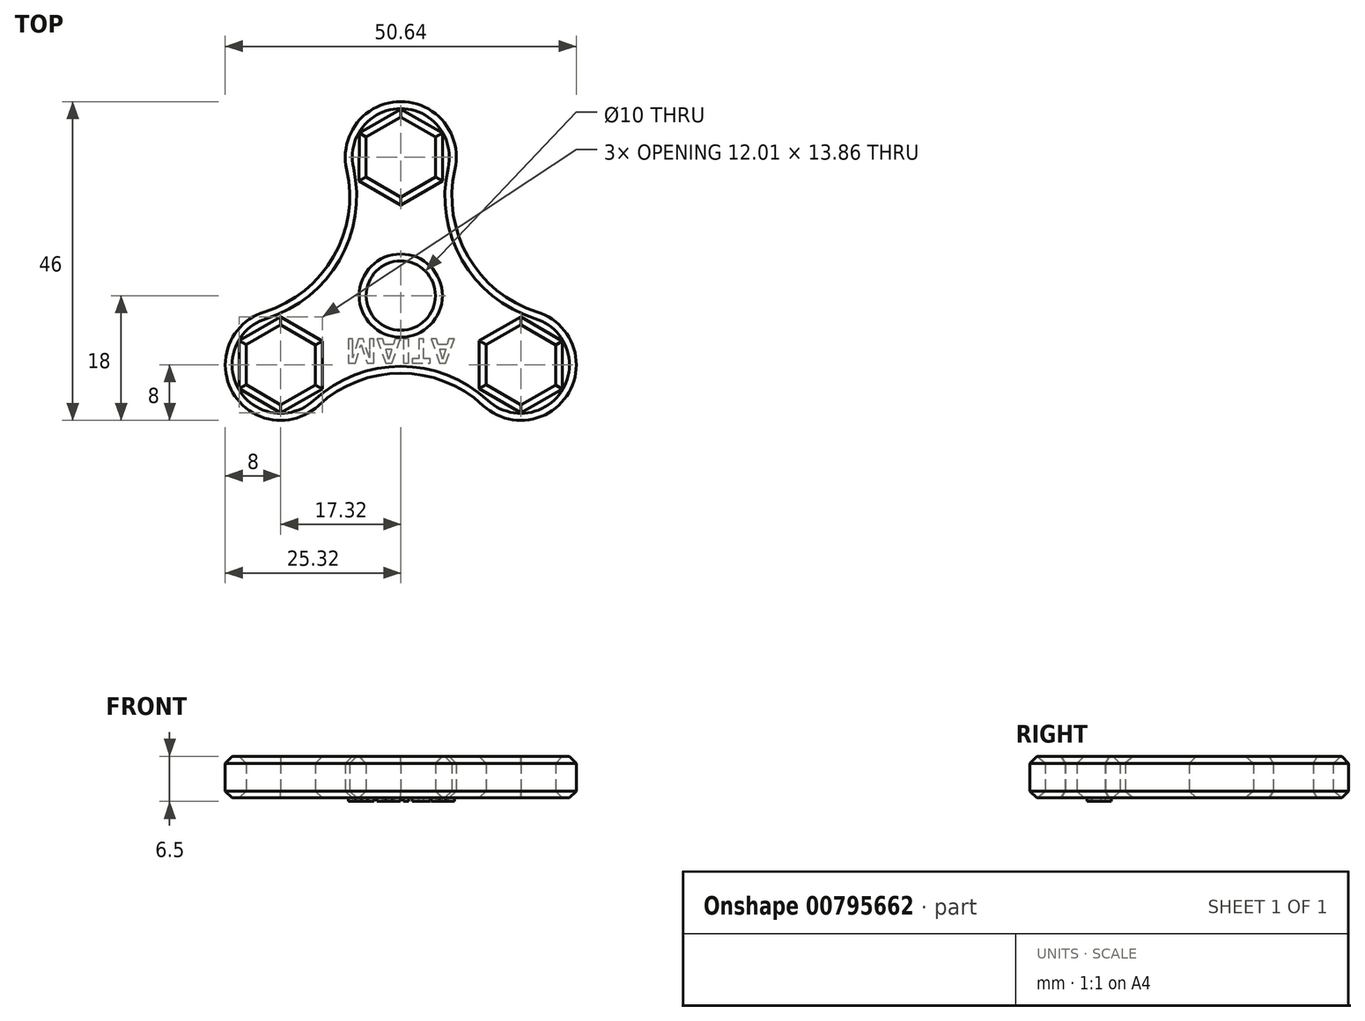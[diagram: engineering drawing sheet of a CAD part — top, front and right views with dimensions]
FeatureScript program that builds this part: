
annotation { "Feature Type Name" : "Feature", "Feature Type Description" : "" }
export const myFeature = defineFeature(function(context is Context, id is Id, definition is map)
    precondition{}
    {
        {
            var Q0;
            Q0=qCreatedBy(makeId("Top.planeOp"),FACE);
            var sketch = newSketch(context, id + "F0", { "sketchPlane" : qUnion([Q0])});
            skCircle(sketch, "E0", {"center": v(0, 0) * mm, "radius": 20 * mm, "construction": true});
            skCircle(sketch, "E1", {"center": v(0, 0) * mm, "radius": 5 * mm});
            skCircle(sketch, "E2.cCircle", {"center": v(0, 20) * mm, "radius": 5 * mm, "construction": true});
            skLineSegment(sketch, "E2.0", {"start": v(0, 25.77) * mm, "end": v(5, 22.88) * mm});
            skLineSegment(sketch, "E2.1", {"start": v(5, 22.88) * mm, "end": v(5, 17.1) * mm});
            skLineSegment(sketch, "E2.2", {"start": v(5, 17.1) * mm, "end": v(0, 14.23) * mm});
            skLineSegment(sketch, "E2.3", {"start": v(0, 14.23) * mm, "end": v(-5, 17.12) * mm});
            skLineSegment(sketch, "E2.4", {"start": v(-5, 17.12) * mm, "end": v(-5, 22.9) * mm});
            skLineSegment(sketch, "E2.5", {"start": v(-5, 22.9) * mm, "end": v(0, 25.77) * mm});
            skPoint(sketch, "E2.0.midPoint", {"position": v(2.5, 24.33) * mm});
            skCircle(sketch, "E3", {"center": v(0, 20) * mm, "radius": 8 * mm});
            skCircle(sketch, "E4", {"center": v(0, 0) * mm, "radius": 8 * mm});
            skCircle(sketch, "E5.1.0", {"center": v(-17.32, -10) * mm, "radius": 8 * mm});
            skLineSegment(sketch, "E5.1.1", {"start": v(-17.33, -15.77) * mm, "end": v(-22.32, -12.88) * mm});
            skLineSegment(sketch, "E5.1.2", {"start": v(-12.32, -12.9) * mm, "end": v(-17.33, -15.77) * mm});
            skLineSegment(sketch, "E5.1.3", {"start": v(-12.32, -7.12) * mm, "end": v(-12.32, -12.9) * mm});
            skLineSegment(sketch, "E5.1.4", {"start": v(-17.31, -4.23) * mm, "end": v(-12.32, -7.12) * mm});
            skLineSegment(sketch, "E5.1.5", {"start": v(-22.32, -7.1) * mm, "end": v(-17.31, -4.23) * mm});
            skLineSegment(sketch, "E5.1.6", {"start": v(-22.32, -12.88) * mm, "end": v(-22.32, -7.1) * mm});
            skCircle(sketch, "E5.2.0", {"center": v(17.32, -10) * mm, "radius": 8 * mm});
            skLineSegment(sketch, "E5.2.1", {"start": v(22.32, -7.12) * mm, "end": v(22.32, -12.9) * mm});
            skLineSegment(sketch, "E5.2.2", {"start": v(17.33, -4.23) * mm, "end": v(22.32, -7.12) * mm});
            skLineSegment(sketch, "E5.2.3", {"start": v(12.32, -7.1) * mm, "end": v(17.33, -4.23) * mm});
            skLineSegment(sketch, "E5.2.4", {"start": v(12.32, -12.88) * mm, "end": v(12.32, -7.1) * mm});
            skLineSegment(sketch, "E5.2.5", {"start": v(17.31, -15.77) * mm, "end": v(12.32, -12.88) * mm});
            skLineSegment(sketch, "E5.2.6", {"start": v(22.32, -12.9) * mm, "end": v(17.31, -15.77) * mm});
            skArc(sketch, "E6", {"start": v(-19.69, -2.36) * mm, "mid": v(-9.71, 5.6) * mm, "end": v(-7.8, 18.23) * mm});
            skArc(sketch, "E7.1.0", {"start": v(11.89, -15.87) * mm, "mid": v(0, -11.21) * mm, "end": v(-11.89, -15.87) * mm});
            skArc(sketch, "E7.2.0", {"start": v(7.8, 18.23) * mm, "mid": v(9.71, 5.6) * mm, "end": v(19.69, -2.36) * mm});
            skSolve(sketch);
        }
        {
            var Q0;
            Q0=makeQuery(id+"F0.imprint","IMPRINT",FACE,{"disambiguationData":[TD([[makeQuery(id+"F0.imprint","IMPRINT",EDGE,{"derivedFrom":sQuery(id+"F0.wireOp",EDGE,"E5.1.1")}),1.0]])]});
            var Q1;
            Q1=makeQuery(id+"F0.imprint","IMPRINT",FACE,{"disambiguationData":[TD([[makeQuery(id+"F0.imprint","IMPRINT",EDGE,{"derivedFrom":sQuery(id+"F0.wireOp",EDGE,"E4")}),-1.0]])]});
            var Q2;
            Q2=makeQuery(id+"F0.imprint","IMPRINT",FACE,{"disambiguationData":[TD([[makeQuery(id+"F0.imprint","IMPRINT",EDGE,{"derivedFrom":sQuery(id+"F0.wireOp",EDGE,"E1")}),-1.0]])]});
            var Q3;
            Q3=makeQuery(id+"F0.imprint","IMPRINT",FACE,{"disambiguationData":[TD([[makeQuery(id+"F0.imprint","IMPRINT",EDGE,{"derivedFrom":sQuery(id+"F0.wireOp",EDGE,"E5.2.1")}),1.0]])]});
            var Q4;
            Q4=makeQuery(id+"F0.imprint","IMPRINT",FACE,{"disambiguationData":[TD([[makeQuery(id+"F0.imprint","IMPRINT",EDGE,{"derivedFrom":sQuery(id+"F0.wireOp",EDGE,"E2.0")}),1.0]])]});
            extrude(context, id + "F1", {"entities" : qUnion([Q0, Q1, Q2, Q3, Q4]), "depth" : 6 * mm, "offsetDistance" : 25 * mm});
        }
        {
            var Q0;
            Q0=makeQuery(id+"F1.opExtrude","CAP_EDGE",EDGE,{"disambiguationData":[OSD([sQuery(id+"F0.wireOp",EDGE,"E5.1.0")])],"isStart":false});
            var Q1;
            Q1=makeQuery(id+"F1.opExtrude","CAP_EDGE",EDGE,{"disambiguationData":[OSD([sQuery(id+"F0.wireOp",EDGE,"E7.1.0")])],"isStart":true});
            var Q2;
            Q2=makeQuery(id+"F1.opExtrude","CAP_EDGE",EDGE,{"disambiguationData":[OSD([sQuery(id+"F0.wireOp",EDGE,"E1")])],"isStart":false});
            var Q3;
            Q3=makeQuery(id+"F1.opExtrude","CAP_EDGE",EDGE,{"disambiguationData":[OSD([sQuery(id+"F0.wireOp",EDGE,"E5.2.3")])],"isStart":false});
            var Q4;
            Q4=makeQuery(id+"F1.opExtrude","CAP_EDGE",EDGE,{"disambiguationData":[OSD([sQuery(id+"F0.wireOp",EDGE,"E5.2.4")])],"isStart":false});
            var Q5;
            Q5=makeQuery(id+"F1.opExtrude","CAP_EDGE",EDGE,{"disambiguationData":[OSD([sQuery(id+"F0.wireOp",EDGE,"E5.2.5")])],"isStart":false});
            var Q6;
            Q6=makeQuery(id+"F1.opExtrude","CAP_EDGE",EDGE,{"disambiguationData":[OSD([sQuery(id+"F0.wireOp",EDGE,"E5.2.6")])],"isStart":false});
            var Q7;
            Q7=makeQuery(id+"F1.opExtrude","CAP_EDGE",EDGE,{"disambiguationData":[OSD([sQuery(id+"F0.wireOp",EDGE,"E5.2.1")])],"isStart":false});
            var Q8;
            Q8=makeQuery(id+"F1.opExtrude","CAP_EDGE",EDGE,{"disambiguationData":[OSD([sQuery(id+"F0.wireOp",EDGE,"E5.2.2")])],"isStart":false});
            var Q9;
            Q9=makeQuery(id+"F1.opExtrude","CAP_EDGE",EDGE,{"disambiguationData":[OSD([sQuery(id+"F0.wireOp",EDGE,"E2.2")])],"isStart":false});
            var Q10;
            Q10=makeQuery(id+"F1.opExtrude","CAP_EDGE",EDGE,{"disambiguationData":[OSD([sQuery(id+"F0.wireOp",EDGE,"E2.3")])],"isStart":false});
            var Q11;
            Q11=makeQuery(id+"F1.opExtrude","CAP_EDGE",EDGE,{"disambiguationData":[OSD([sQuery(id+"F0.wireOp",EDGE,"E2.4")])],"isStart":false});
            var Q12;
            Q12=makeQuery(id+"F1.opExtrude","CAP_EDGE",EDGE,{"disambiguationData":[OSD([sQuery(id+"F0.wireOp",EDGE,"E2.5")])],"isStart":false});
            var Q13;
            Q13=makeQuery(id+"F1.opExtrude","CAP_EDGE",EDGE,{"disambiguationData":[OSD([sQuery(id+"F0.wireOp",EDGE,"E2.0")])],"isStart":false});
            var Q14;
            Q14=makeQuery(id+"F1.opExtrude","CAP_EDGE",EDGE,{"disambiguationData":[OSD([sQuery(id+"F0.wireOp",EDGE,"E2.1")])],"isStart":false});
            var Q15;
            Q15=makeQuery(id+"F1.opExtrude","CAP_EDGE",EDGE,{"disambiguationData":[OSD([sQuery(id+"F0.wireOp",EDGE,"E5.1.4")])],"isStart":false});
            var Q16;
            Q16=makeQuery(id+"F1.opExtrude","CAP_EDGE",EDGE,{"disambiguationData":[OSD([sQuery(id+"F0.wireOp",EDGE,"E5.1.5")])],"isStart":false});
            var Q17;
            Q17=makeQuery(id+"F1.opExtrude","CAP_EDGE",EDGE,{"disambiguationData":[OSD([sQuery(id+"F0.wireOp",EDGE,"E5.1.6")])],"isStart":false});
            var Q18;
            Q18=makeQuery(id+"F1.opExtrude","CAP_EDGE",EDGE,{"disambiguationData":[OSD([sQuery(id+"F0.wireOp",EDGE,"E5.1.1")])],"isStart":false});
            var Q19;
            Q19=makeQuery(id+"F1.opExtrude","CAP_EDGE",EDGE,{"disambiguationData":[OSD([sQuery(id+"F0.wireOp",EDGE,"E5.1.2")])],"isStart":false});
            var Q20;
            Q20=makeQuery(id+"F1.opExtrude","CAP_EDGE",EDGE,{"disambiguationData":[OSD([sQuery(id+"F0.wireOp",EDGE,"E5.1.3")])],"isStart":false});
            var Q21;
            Q21=makeQuery(id+"F1.opExtrude","CAP_EDGE",EDGE,{"disambiguationData":[OSD([sQuery(id+"F0.wireOp",EDGE,"E5.1.4")])],"isStart":true});
            var Q22;
            Q22=makeQuery(id+"F1.opExtrude","CAP_EDGE",EDGE,{"disambiguationData":[OSD([sQuery(id+"F0.wireOp",EDGE,"E5.1.5")])],"isStart":true});
            var Q23;
            Q23=makeQuery(id+"F1.opExtrude","CAP_EDGE",EDGE,{"disambiguationData":[OSD([sQuery(id+"F0.wireOp",EDGE,"E5.1.6")])],"isStart":true});
            var Q24;
            Q24=makeQuery(id+"F1.opExtrude","CAP_EDGE",EDGE,{"disambiguationData":[OSD([sQuery(id+"F0.wireOp",EDGE,"E5.1.1")])],"isStart":true});
            var Q25;
            Q25=makeQuery(id+"F1.opExtrude","CAP_EDGE",EDGE,{"disambiguationData":[OSD([sQuery(id+"F0.wireOp",EDGE,"E5.1.2")])],"isStart":true});
            var Q26;
            Q26=makeQuery(id+"F1.opExtrude","CAP_EDGE",EDGE,{"disambiguationData":[OSD([sQuery(id+"F0.wireOp",EDGE,"E5.1.3")])],"isStart":true});
            var Q27;
            Q27=makeQuery(id+"F1.opExtrude","CAP_EDGE",EDGE,{"disambiguationData":[OSD([sQuery(id+"F0.wireOp",EDGE,"E5.2.4")])],"isStart":true});
            var Q28;
            Q28=makeQuery(id+"F1.opExtrude","CAP_EDGE",EDGE,{"disambiguationData":[OSD([sQuery(id+"F0.wireOp",EDGE,"E5.2.5")])],"isStart":true});
            var Q29;
            Q29=makeQuery(id+"F1.opExtrude","CAP_EDGE",EDGE,{"disambiguationData":[OSD([sQuery(id+"F0.wireOp",EDGE,"E5.2.6")])],"isStart":true});
            var Q30;
            Q30=makeQuery(id+"F1.opExtrude","CAP_EDGE",EDGE,{"disambiguationData":[OSD([sQuery(id+"F0.wireOp",EDGE,"E5.2.1")])],"isStart":true});
            var Q31;
            Q31=makeQuery(id+"F1.opExtrude","CAP_EDGE",EDGE,{"disambiguationData":[OSD([sQuery(id+"F0.wireOp",EDGE,"E5.2.2")])],"isStart":true});
            var Q32;
            Q32=makeQuery(id+"F1.opExtrude","CAP_EDGE",EDGE,{"disambiguationData":[OSD([sQuery(id+"F0.wireOp",EDGE,"E5.2.3")])],"isStart":true});
            var Q33;
            Q33=makeQuery(id+"F1.opExtrude","CAP_EDGE",EDGE,{"disambiguationData":[OSD([sQuery(id+"F0.wireOp",EDGE,"E2.2")])],"isStart":true});
            var Q34;
            Q34=makeQuery(id+"F1.opExtrude","CAP_EDGE",EDGE,{"disambiguationData":[OSD([sQuery(id+"F0.wireOp",EDGE,"E2.3")])],"isStart":true});
            var Q35;
            Q35=makeQuery(id+"F1.opExtrude","CAP_EDGE",EDGE,{"disambiguationData":[OSD([sQuery(id+"F0.wireOp",EDGE,"E2.4")])],"isStart":true});
            var Q36;
            Q36=makeQuery(id+"F1.opExtrude","CAP_EDGE",EDGE,{"disambiguationData":[OSD([sQuery(id+"F0.wireOp",EDGE,"E2.5")])],"isStart":true});
            var Q37;
            Q37=makeQuery(id+"F1.opExtrude","CAP_EDGE",EDGE,{"disambiguationData":[OSD([sQuery(id+"F0.wireOp",EDGE,"E2.0")])],"isStart":true});
            var Q38;
            Q38=makeQuery(id+"F1.opExtrude","CAP_EDGE",EDGE,{"disambiguationData":[OSD([sQuery(id+"F0.wireOp",EDGE,"E2.1")])],"isStart":true});
            var Q39;
            Q39=makeQuery(id+"F1.opExtrude","CAP_EDGE",EDGE,{"disambiguationData":[OSD([sQuery(id+"F0.wireOp",EDGE,"E1")])],"isStart":true});
            chamfer(context, id + "F2", {"entities" : qUnion([Q0, Q1, Q2, Q3, Q4, Q5, Q6, Q7, Q8, Q9, Q10, Q11, Q12, Q13, Q14, Q15, Q16, Q17, Q18, Q19, Q20, Q21, Q22, Q23, Q24, Q25, Q26, Q27, Q28, Q29, Q30, Q31, Q32, Q33, Q34, Q35, Q36, Q37, Q38, Q39]), "width" : 1 * mm, "tangentPropagation" : true});
        }
        {
            var Q0;
            Q0=makeQuery(id+"F1.opExtrude","CAP_FACE",FACE,{"disambiguationData":[OSD([sQuery(id+"F0.wireOp",EDGE,"E1"),sQuery(id+"F0.wireOp",EDGE,"E2.0"),sQuery(id+"F0.wireOp",EDGE,"E2.1"),sQuery(id+"F0.wireOp",EDGE,"E2.2"),sQuery(id+"F0.wireOp",EDGE,"E2.3"),sQuery(id+"F0.wireOp",EDGE,"E2.4"),sQuery(id+"F0.wireOp",EDGE,"E2.5"),sQuery(id+"F0.wireOp",EDGE,"E3"),sQuery(id+"F0.wireOp",EDGE,"E5.1.0"),sQuery(id+"F0.wireOp",EDGE,"E5.1.1"),sQuery(id+"F0.wireOp",EDGE,"E5.1.2"),sQuery(id+"F0.wireOp",EDGE,"E5.1.3"),sQuery(id+"F0.wireOp",EDGE,"E5.1.4"),sQuery(id+"F0.wireOp",EDGE,"E5.1.5"),sQuery(id+"F0.wireOp",EDGE,"E5.1.6"),sQuery(id+"F0.wireOp",EDGE,"E5.2.0"),sQuery(id+"F0.wireOp",EDGE,"E5.2.1"),sQuery(id+"F0.wireOp",EDGE,"E5.2.2"),sQuery(id+"F0.wireOp",EDGE,"E5.2.3"),sQuery(id+"F0.wireOp",EDGE,"E5.2.4"),sQuery(id+"F0.wireOp",EDGE,"E5.2.5"),sQuery(id+"F0.wireOp",EDGE,"E5.2.6"),sQuery(id+"F0.wireOp",EDGE,"E6"),sQuery(id+"F0.wireOp",EDGE,"E7.1.0"),sQuery(id+"F0.wireOp",EDGE,"E7.2.0")])],"isStart":true});
            var sketch = newSketch(context, id + "F3", { "sketchPlane" : qUnion([Q0])});
            skText(sketch, "E8", { "text": "MAITA", "fontName": "OpenSans-Bold.ttf"});
            const initialGuessF3  = {"E8": [-0.008, 0.00625, 1, 0, 0.0035]};
            skSetInitialGuess(sketch, initialGuessF3);
            skSolve(sketch);
        }
        {
            var Q0;
            Q0=makeQuery(id+"F3.imprint","IMPRINT",FACE,{"disambiguationData":[TD([[makeQuery(id+"F3.imprint","IMPRINT",EDGE,{"derivedFrom":sQuery(id+"F3.wireOp",EDGE,"E8.sketch_text.stroke-31")}),-1.0]])]});
            var Q1;
            Q1=makeQuery(id+"F3.imprint","IMPRINT",FACE,{"disambiguationData":[TD([[makeQuery(id+"F3.imprint","IMPRINT",EDGE,{"derivedFrom":sQuery(id+"F3.wireOp",EDGE,"E8.sketch_text.stroke-35")}),-1.0]])]});
            var Q2;
            Q2=makeQuery(id+"F3.imprint","IMPRINT",FACE,{"disambiguationData":[TD([[makeQuery(id+"F3.imprint","IMPRINT",EDGE,{"derivedFrom":sQuery(id+"F3.wireOp",EDGE,"E8.sketch_text.stroke-43")}),-1.0]])]});
            var Q3;
            Q3=makeQuery(id+"F3.imprint","IMPRINT",FACE,{"disambiguationData":[TD([[makeQuery(id+"F3.imprint","IMPRINT",EDGE,{"derivedFrom":sQuery(id+"F3.wireOp",EDGE,"E8.sketch_text.stroke-19")}),-1.0]])]});
            var Q4;
            Q4=makeQuery(id+"F3.imprint","IMPRINT",FACE,{"disambiguationData":[TD([[makeQuery(id+"F3.imprint","IMPRINT",EDGE,{"derivedFrom":sQuery(id+"F3.wireOp",EDGE,"E8.sketch_text.stroke-0")}),-1.0]])]});
            extrude(context, id + "F4", {"entities" : qUnion([Q0, Q1, Q2, Q3, Q4]), "operationType" : NewBodyOperationType.ADD, "depth" : .5 * mm, "offsetDistance" : 25 * mm});
        }
    });
